# Revit family: 1
name_source: partatom
category: Plumbing Fixtures
revit_build: Autodesk Revit 2018 (Build: 20190510_1515(x64)
units: mm (PartAtom-declared; Revit-internal decimal feet)

## family parameters
Always vertical = No
Cut with Voids When Loaded = No
OmniClass Number = 23.31.13.00
OmniClass Title = Sinks
Part Type = Normal
Room Calculation Point = No
Round Connector Dimension = Use Diameter
Shared = No
Work Plane-Based = Yes

## types (2) — shared parameters
BIMobject category = Wash basins
BIMobject category code = wash-basins
BIMobject main category = Sanitary
BIMobject main category code = sanitary
Brand url = http://www.duravit.com
Connector Description = Water outlet
Default Elevation = 1219.2 mm  [stored 4 ft]
Design country = Germany
ETIM classification = EC011550 | Washbasin
Edition number = 1
IFC Classification = Sanitary Terminal
Installation instructions = https://duravit-public-assets.s3.eu-central-1.amazonaws.com
Manufacturer = Duravit
Manufacturer name = DURAVIT AG
Masterformat 2014 Code = 22 41 16.13
Masterformat 2014 Description = Residential Lavatories
Material main = Ceramics
Model = DuraStyle Washbowl 600 mm - 034960
OmniClass Code = 23-31 13 00
OmniClass Description = Sinks
Outlet Diameter = 32 mm
Product Guid = eb7557a1-61f7-4b1b-ad8f-54d8012408a8
Product SKU = DuraStyle-Washbowl-600-mm-034960
Product certification = http://pro.duravit.com
Product data url = https://bimobject.com
Product family = DuraStyle
Product group = Washbowl
Product name = DuraStyle Washbowl 600 mm - 034960
Product url = http://pro.duravit.com
QR code = http://bimobject.com
Secondary material = Duravit - Metal - 10 - Chrome
Technical description = http://pro.duravit.com
UNSPSC Code = 30181504
URL = https://www.duravit.com
Uniclass 2015 Code = Pr_40_20_96
Uniclass 2015 Name = Wash basins, sinks and troughs
Uniformat II Code = D2010
Uniformat II Description = Plumbing Fixtures
Youtube clip = http://pro.duravit.com

## per-type parameters (varying)
| type | Description | Main material |
| 00 - White Alpin WonderGliss | Duravit DuraStyle Washbowl 600 mm White High Gloss, WonderGliss - 03496000001 | Duravit - Ceramic - 00 - White Alpin WonderGliss |
| 00 - White Alpin | Duravit DuraStyle Washbowl 600 mm White High Gloss - 0349600000 | Duravit - Ceramic - 00 - White Alpin |

note: [stored X ft] marks values corroborated as IEEE doubles in the binary element streams (Revit-internal decimal feet)

## geometry (parser evidence)
native form markers: Sweep x4
no freeform markers — native parametric forms only
